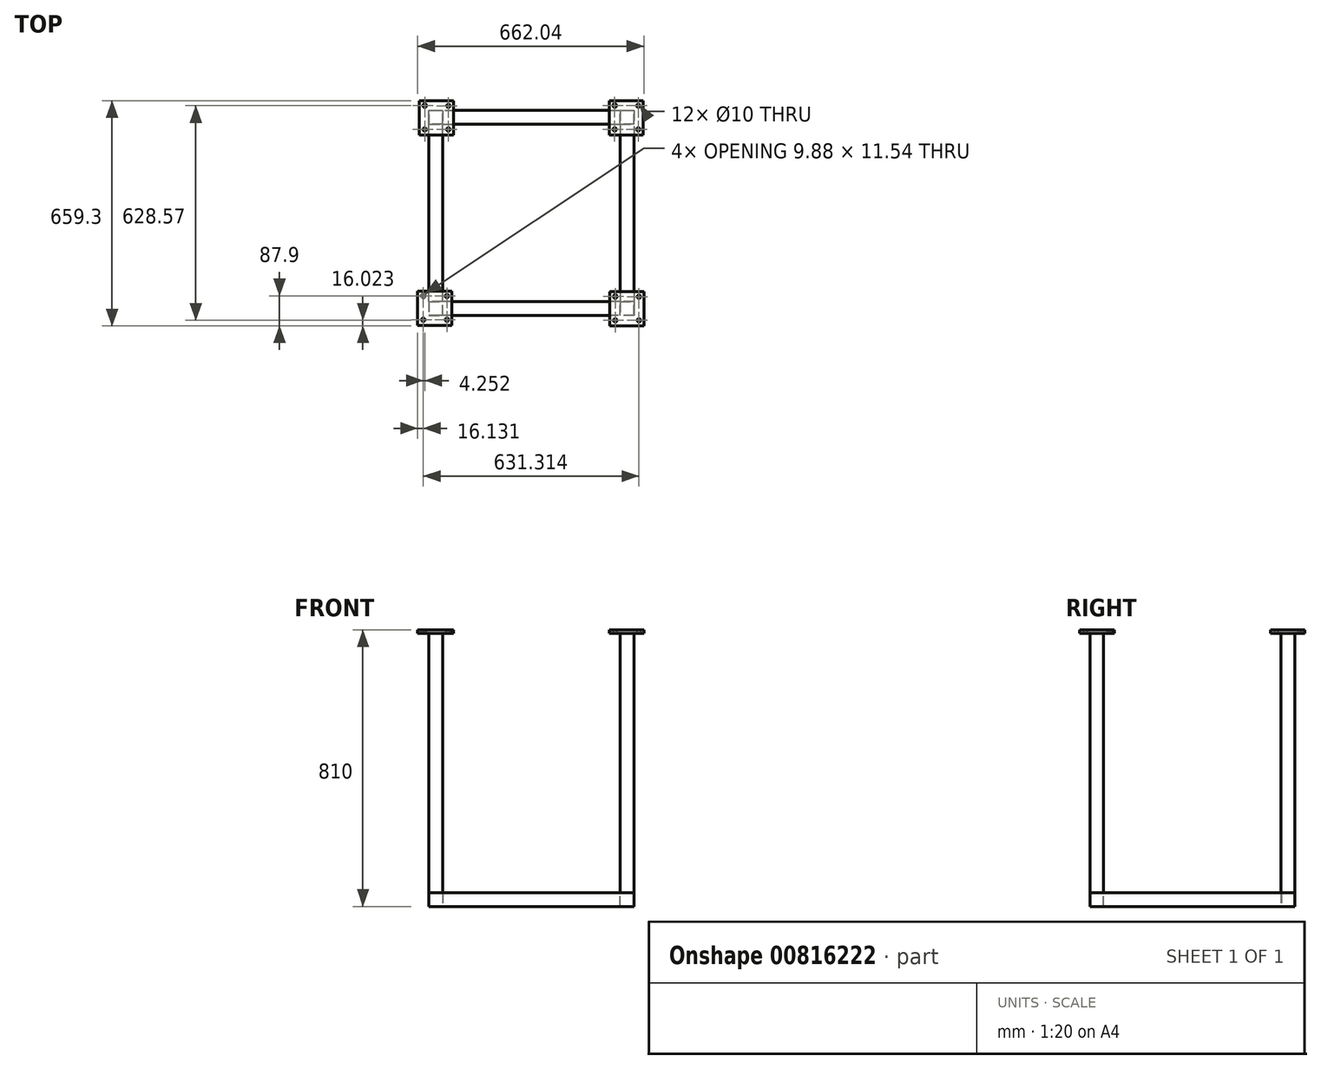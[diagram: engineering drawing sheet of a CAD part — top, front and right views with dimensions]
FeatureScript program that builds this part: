
annotation { "Feature Type Name" : "Feature", "Feature Type Description" : "" }
export const myFeature = defineFeature(function(context is Context, id is Id, definition is map)
    precondition{}
    {
        {
            var Q0;
            Q0=qCreatedBy(makeId("Top.planeOp"),FACE);
            var sketch = newSketch(context, id + "F0", { "sketchPlane" : qUnion([Q0])});
            skLineSegment(sketch, "E0", {"start": v(-1002.53, -89.91) * mm, "end": v(-482.53, -89.91) * mm});
            skLineSegment(sketch, "E1", {"start": v(-482.53, -89.91) * mm, "end": v(-482.53, -609.91) * mm});
            skLineSegment(sketch, "E2", {"start": v(-482.53, -609.91) * mm, "end": v(-1002.53, -609.91) * mm});
            skLineSegment(sketch, "E3", {"start": v(-1002.53, -609.91) * mm, "end": v(-1002.53, -89.91) * mm});
            skLineSegment(sketch, "E4", {"start": v(-1042.53, -49.91) * mm, "end": v(-442.53, -49.91) * mm});
            skLineSegment(sketch, "E5", {"start": v(-442.53, -49.91) * mm, "end": v(-442.53, -649.91) * mm});
            skLineSegment(sketch, "E6", {"start": v(-442.53, -649.91) * mm, "end": v(-1042.53, -649.91) * mm});
            skLineSegment(sketch, "E7", {"start": v(-1042.53, -649.91) * mm, "end": v(-1042.53, -49.91) * mm});
            skSolve(sketch);
        }
        {
            var Q0;
            Q0 = qSketchRegion(id + "F0", true);
            extrude(context, id + "F1", {"entities" : qUnion([Q0]), "depth" : 40 * mm, "offsetDistance" : 25 * mm});
        }
        {
            var Q0;
            Q0=qCreatedBy(makeId("Top.planeOp"),FACE);
            var sketch = newSketch(context, id + "F2", { "sketchPlane" : qUnion([Q0])});
            skLineSegment(sketch, "E8.bottom", {"start": v(-482.97, -50.52) * mm, "end": v(-442.97, -50.52) * mm});
            skLineSegment(sketch, "E8.top", {"start": v(-482.97, -90.52) * mm, "end": v(-442.97, -90.52) * mm});
            skLineSegment(sketch, "E8.left", {"start": v(-482.97, -50.52) * mm, "end": v(-482.97, -90.52) * mm});
            skLineSegment(sketch, "E8.right", {"start": v(-442.97, -50.52) * mm, "end": v(-442.97, -90.52) * mm});
            skLineSegment(sketch, "E9.bottom", {"start": v(-1041.84, -50.52) * mm, "end": v(-1001.84, -50.52) * mm});
            skLineSegment(sketch, "E9.top", {"start": v(-1041.84, -90.52) * mm, "end": v(-1001.84, -90.52) * mm});
            skLineSegment(sketch, "E9.left", {"start": v(-1041.84, -50.52) * mm, "end": v(-1041.84, -90.52) * mm});
            skLineSegment(sketch, "E9.right", {"start": v(-1001.84, -50.52) * mm, "end": v(-1001.84, -90.52) * mm});
            skLineSegment(sketch, "E10.bottom", {"start": v(-482.97, -609.83) * mm, "end": v(-442.97, -609.83) * mm});
            skLineSegment(sketch, "E10.top", {"start": v(-482.97, -649.83) * mm, "end": v(-442.97, -649.83) * mm});
            skLineSegment(sketch, "E10.left", {"start": v(-482.97, -609.83) * mm, "end": v(-482.97, -649.83) * mm});
            skLineSegment(sketch, "E10.right", {"start": v(-442.97, -609.83) * mm, "end": v(-442.97, -649.83) * mm});
            skLineSegment(sketch, "E11.bottom", {"start": v(-1042.78, -609.83) * mm, "end": v(-1002.78, -609.83) * mm});
            skLineSegment(sketch, "E11.top", {"start": v(-1042.78, -649.83) * mm, "end": v(-1002.78, -649.83) * mm});
            skLineSegment(sketch, "E11.left", {"start": v(-1042.78, -609.83) * mm, "end": v(-1042.78, -649.83) * mm});
            skLineSegment(sketch, "E11.right", {"start": v(-1002.78, -609.83) * mm, "end": v(-1002.78, -649.83) * mm});
            skSolve(sketch);
        }
        {
            var Q0;
            Q0 = qSketchRegion(id + "F2", true);
            extrude(context, id + "F3", {"entities" : qUnion([Q0]), "operationType" : NewBodyOperationType.ADD, "depth" : 800 * mm, "offsetDistance" : 25 * mm});
        }
        {
            var Q0;
            Q0=makeQuery(id+"F3.opExtrude","CAP_FACE",FACE,{"disambiguationData":[OSD([sQuery(id+"F2.wireOp",EDGE,"E9.bottom"),sQuery(id+"F2.wireOp",EDGE,"E9.top"),sQuery(id+"F2.wireOp",EDGE,"E9.left"),sQuery(id+"F2.wireOp",EDGE,"E9.right")])],"isStart":false});
            var sketch = newSketch(context, id + "F4", { "sketchPlane" : qUnion([Q0])});
            skLineSegment(sketch, "E12.bottom", {"start": v(-971.18, -121.57) * mm, "end": v(-1071.18, -121.57) * mm});
            skLineSegment(sketch, "E12.top", {"start": v(-971.18, -21.57) * mm, "end": v(-1071.18, -21.57) * mm});
            skLineSegment(sketch, "E12.left", {"start": v(-971.18, -121.57) * mm, "end": v(-971.18, -21.57) * mm});
            skLineSegment(sketch, "E12.right", {"start": v(-1071.18, -121.57) * mm, "end": v(-1071.18, -21.57) * mm});
            skCircle(sketch, "E13", {"center": v(-1055.05, -34.73) * mm, "radius": 5 * mm});
            skCircle(sketch, "E14", {"center": v(-1055.05, -36.27) * mm, "radius": 5 * mm});
            skCircle(sketch, "E15", {"center": v(-985.77, -36.27) * mm, "radius": 5 * mm});
            skCircle(sketch, "E16", {"center": v(-1055.05, -105.54) * mm, "radius": 5 * mm});
            skCircle(sketch, "E17", {"center": v(-985.77, -105.54) * mm, "radius": 5 * mm});
            skLineSegment(sketch, "E18.bottom", {"start": v(-415.09, -121.44) * mm, "end": v(-515.09, -121.44) * mm});
            skLineSegment(sketch, "E18.top", {"start": v(-415.09, -21.44) * mm, "end": v(-515.09, -21.44) * mm});
            skLineSegment(sketch, "E18.left", {"start": v(-415.09, -121.44) * mm, "end": v(-415.09, -21.44) * mm});
            skLineSegment(sketch, "E18.right", {"start": v(-515.09, -121.44) * mm, "end": v(-515.09, -21.44) * mm});
            skCircle(sketch, "E19", {"center": v(-498.96, -34.6) * mm, "radius": 5 * mm});
            skCircle(sketch, "E20", {"center": v(-498.96, -36.15) * mm, "radius": 5 * mm});
            skCircle(sketch, "E21", {"center": v(-429.68, -36.15) * mm, "radius": 5 * mm});
            skCircle(sketch, "E22", {"center": v(-498.96, -105.42) * mm, "radius": 5 * mm});
            skCircle(sketch, "E23", {"center": v(-429.68, -105.42) * mm, "radius": 5 * mm});
            skLineSegment(sketch, "E24.bottom", {"start": v(-413.4, -680.74) * mm, "end": v(-513.4, -680.74) * mm});
            skLineSegment(sketch, "E24.top", {"start": v(-413.4, -580.74) * mm, "end": v(-513.4, -580.74) * mm});
            skLineSegment(sketch, "E24.left", {"start": v(-413.4, -680.74) * mm, "end": v(-413.4, -580.74) * mm});
            skLineSegment(sketch, "E24.right", {"start": v(-513.4, -680.74) * mm, "end": v(-513.4, -580.74) * mm});
            skCircle(sketch, "E25", {"center": v(-497.26, -593.9) * mm, "radius": 5 * mm});
            skCircle(sketch, "E26", {"center": v(-497.26, -595.44) * mm, "radius": 5 * mm});
            skCircle(sketch, "E27", {"center": v(-427.98, -595.44) * mm, "radius": 5 * mm});
            skCircle(sketch, "E28", {"center": v(-497.26, -664.72) * mm, "radius": 5 * mm});
            skCircle(sketch, "E29", {"center": v(-427.98, -664.72) * mm, "radius": 5 * mm});
            skLineSegment(sketch, "E30.bottom", {"start": v(-975.43, -678.9) * mm, "end": v(-1075.43, -678.9) * mm});
            skLineSegment(sketch, "E30.top", {"start": v(-975.43, -578.9) * mm, "end": v(-1075.43, -578.9) * mm});
            skLineSegment(sketch, "E30.left", {"start": v(-975.43, -678.9) * mm, "end": v(-975.43, -578.9) * mm});
            skLineSegment(sketch, "E30.right", {"start": v(-1075.43, -678.9) * mm, "end": v(-1075.43, -578.9) * mm});
            skCircle(sketch, "E31", {"center": v(-1059.3, -592.07) * mm, "radius": 5 * mm});
            skCircle(sketch, "E32", {"center": v(-1059.3, -593.6) * mm, "radius": 5 * mm});
            skCircle(sketch, "E33", {"center": v(-990.02, -593.6) * mm, "radius": 5 * mm});
            skCircle(sketch, "E34", {"center": v(-1059.3, -662.89) * mm, "radius": 5 * mm});
            skCircle(sketch, "E35", {"center": v(-990.02, -662.89) * mm, "radius": 5 * mm});
            skSolve(sketch);
        }
        {
            var Q0;
            Q0 = qSketchRegion(id + "F4", true);
            extrude(context, id + "F5", {"entities" : qUnion([Q0]), "operationType" : NewBodyOperationType.ADD, "depth" : 10 * mm, "offsetDistance" : 25 * mm});
        }
    });
